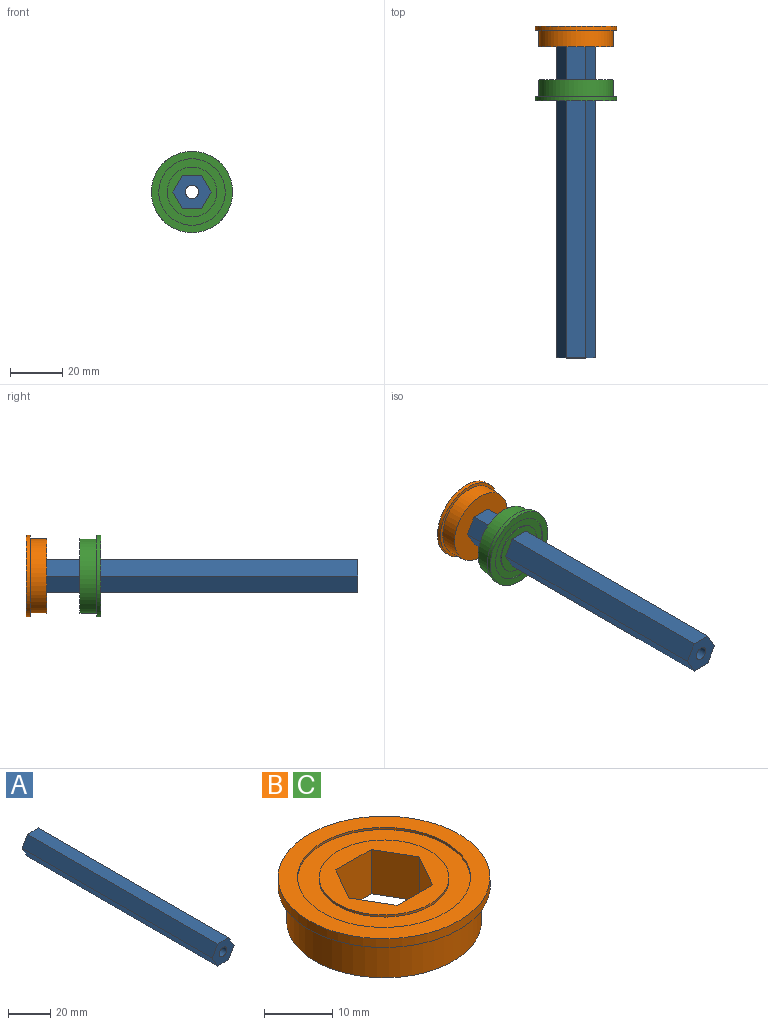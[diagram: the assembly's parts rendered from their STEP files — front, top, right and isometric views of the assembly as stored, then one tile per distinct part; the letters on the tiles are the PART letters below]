
ASSEMBLY  parts=3 mates=2
PART A: 9 faces, bbox 14.7x127x12.7 mm
  f0: plane 127x6.35mm, normal (-0.87,0,-0.5), area 931.2mm2, adj f1,f6,f7,f8
  f1: plane 127x7.33mm, normal (0,0,-1), area 931.2mm2, adj f0,f2,f7,f8
  f2: plane 127x6.35mm, normal (0.87,0,-0.5), area 931.2mm2, adj f1,f3,f7,f8
  f3: plane 127x6.35mm, normal (0.87,0,0.5), area 931.2mm2, adj f2,f4,f7,f8
  f4: plane 127x7.33mm, normal (0,0,1), area 931.2mm2, adj f3,f6,f7,f8
  f5: cylinder r=2.55mm len=127mm, axis (0,1,0), area 2037mm2, adj f7,f8
  f6: plane 127x6.35mm, normal (-0.87,0,0.5), area 931.2mm2, adj f0,f4,f7,f8
  f7: plane 14.66x12.7mm, normal (0,-1,0), area 119.2mm2, adj f0,f1,f2,f3,f4,f5,f6
  f8: plane 14.66x12.7mm, normal (0,1,0), area 119.2mm2, adj f0,f1,f2,f3,f4,f5,f6
PART B: 15 faces, bbox 31.1x31.1x7.9 mm
  f0: cylinder r=12.7mm len=25.4mm, axis (0,0,1), area 30.4mm2, adj f7,f8
  f1: cylinder r=15.56mm len=31.12mm, axis (0,0,1), area 155.2mm2, adj f6,f7
  f2: cylinder r=14.27mm len=28.55mm, axis (0,0,1), area 569.5mm2, adj f5,f6
  f3: cylinder r=9.53mm len=19.05mm, axis (0,0,1), area 22.8mm2, adj f4,f8
  f4: plane 19.05x19.05mm, normal (0,0,1), area 144.9mm2, adj f3,f9,f10,f11,f12,f13,f14
  f5: plane 28.55x28.55mm, normal (0,0,-1), area 500mm2, adj f2,f9,f10,f11,f12,f13,f14
  f6: plane 31.12x31.12mm, normal (0,0,-1), area 120.2mm2, adj f1,f2
  f7: plane 31.12x31.12mm, normal (0,0,1), area 253.7mm2, adj f0,f1
  f8: plane 25.4x25.4mm, normal (0,0,1), area 221.7mm2, adj f0,f3
  f9: plane 7.94x6.36mm, normal (-0.87,-0.5,0), area 58.3mm2, adj f4,f5,f10,f14
  f10: plane 7.94x6.36mm, normal (-0.87,0.5,0), area 58.3mm2, adj f4,f5,f9,f11
  f11: plane 7.94x7.34mm, normal (0,1,0), area 58.3mm2, adj f4,f5,f10,f12
  f12: plane 7.94x6.36mm, normal (0.87,0.5,0), area 58.3mm2, adj f4,f5,f11,f13
  f13: plane 7.94x6.36mm, normal (0.87,-0.5,0), area 58.3mm2, adj f4,f5,f12,f14
  f14: plane 7.94x7.34mm, normal (0,-1,0), area 58.3mm2, adj f4,f5,f9,f13
PART C: same geometry as B
PLACE A t=(-269.07,-85.69,-154.87)mm
PLACE B rot(axis=(-1,0,0),90deg) t=(-269.07,-30.12,-154.87)mm
PLACE C rot(axis=(1,0,0),90deg) t=(-269.07,-42.82,-154.87)mm
MATE fastened C.f0 <-> B.f0  axis (0,1,0) through (-269.07,-49.17,-154.87)mm
MATE fastened B.f0 <-> A.f5  axis (0,1,0) through (-269.07,-22.19,-154.87)mm
